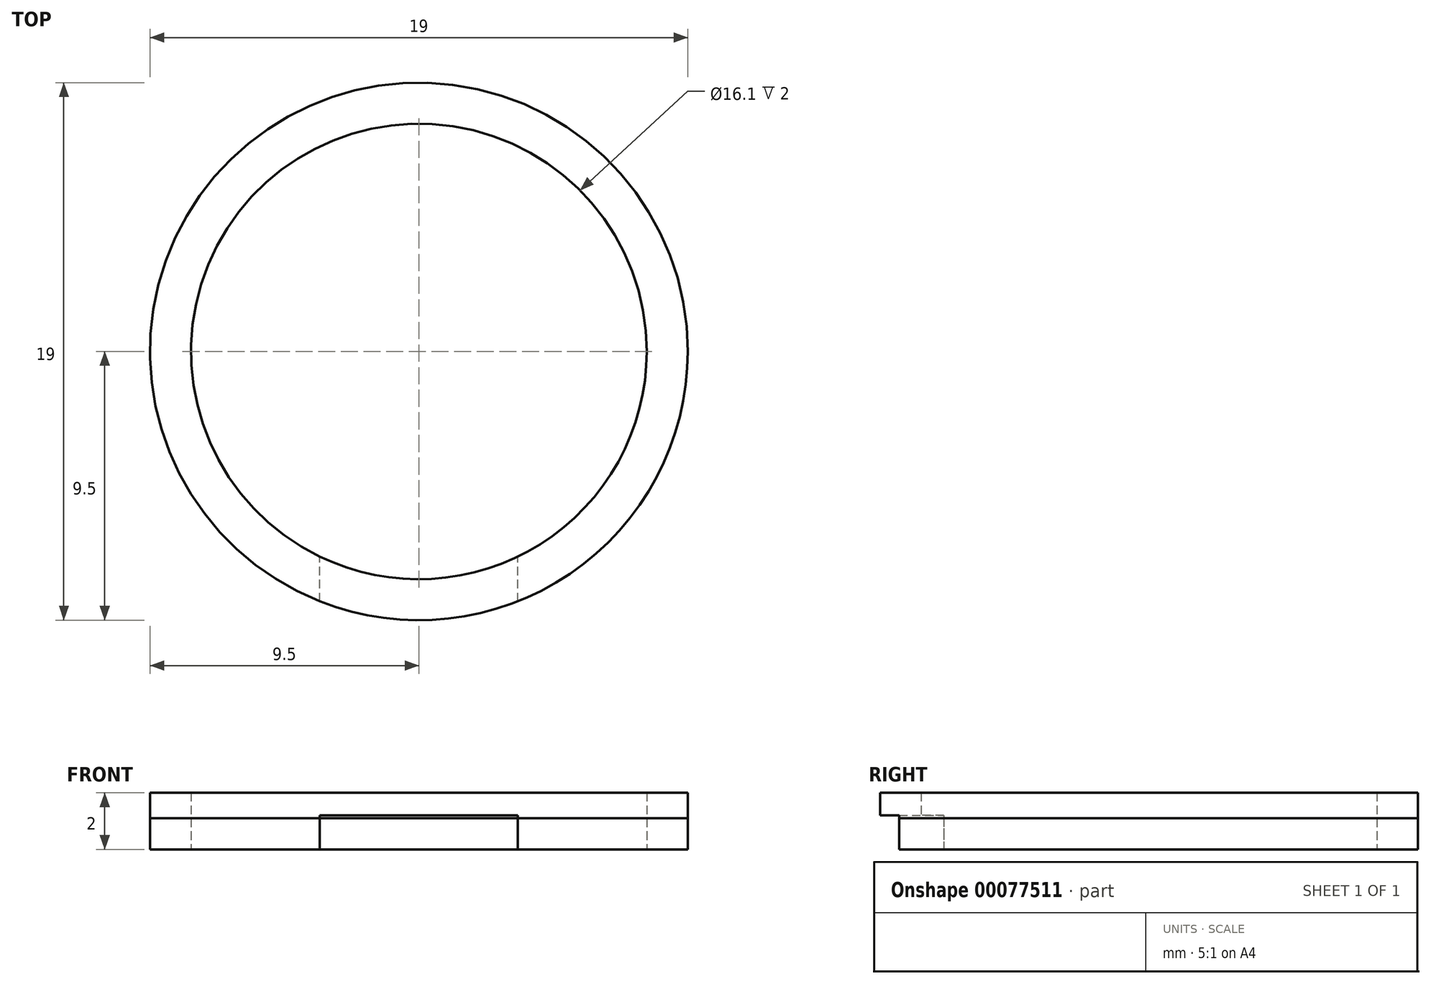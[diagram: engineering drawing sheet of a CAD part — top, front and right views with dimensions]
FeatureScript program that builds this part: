
annotation { "Feature Type Name" : "Feature", "Feature Type Description" : "" }
export const myFeature = defineFeature(function(context is Context, id is Id, definition is map)
    precondition{}
    {
        {
            var Q0;
            Q0=qCreatedBy(makeId("Top.planeOp"),FACE);
            var sketch = newSketch(context, id + "F0", { "sketchPlane" : qUnion([Q0])});
            skCircle(sketch, "E0", {"center": v(0, 0) * mm, "radius": 8.05 * mm});
            skCircle(sketch, "E1", {"center": v(0, 0) * mm, "radius": 9.5 * mm});
            skSolve(sketch);
        }
        {
            var Q0;
            Q0=makeQuery(id+"F0.imprint","IMPRINT",FACE,{"disambiguationData":[TD([[makeQuery(id+"F0.imprint","IMPRINT",EDGE,{"derivedFrom":sQuery(id+"F0.wireOp",EDGE,"E0")}),-1.0]])]});
            extrude(context, id + "F1", {"entities" : qUnion([Q0]), "depth" : 1.1 * mm});
        }
        {
            var Q0;
            Q0=makeQuery(id+"F0.imprint","IMPRINT",FACE,{"disambiguationData":[TD([[makeQuery(id+"F0.imprint","IMPRINT",EDGE,{"derivedFrom":sQuery(id+"F0.wireOp",EDGE,"E0")}),-1.0]])]});
            extrude(context, id + "F2", {"entities" : qUnion([Q0]), "depth" : 2 * mm});
        }
        {
            var Q0;
            Q0=makeQuery(id+"F2.opExtrude","CAP_FACE",FACE,{"disambiguationData":[OSD([sQuery(id+"F0.wireOp",EDGE,"E0"),sQuery(id+"F0.wireOp",EDGE,"E1")])],"isStart":true});
            var sketch = newSketch(context, id + "F3", { "sketchPlane" : qUnion([Q0])});
            skLineSegment(sketch, "E2", {"start": v(-3.5, 8.83) * mm, "end": v(-3.5, 7.25) * mm});
            skLineSegment(sketch, "E3", {"start": v(3.5, 8.83) * mm, "end": v(3.5, 7.25) * mm});
            skSolve(sketch);
        }
        {
            var Q0;
            {var subQ2=sQuery(id+"F3.wireOp",EDGE,"E2");Q0=makeQuery(id+"F3.imprint","IMPRINT",FACE,{"disambiguationData":[TD([[makeQuery(id+"F3.imprint","IMPRINT",EDGE,{"derivedFrom":subQ2}),1.0]])]});}
            extrude(context, id + "F4", {"entities" : qUnion([Q0]), "operationType" : NewBodyOperationType.REMOVE, "oppositeDirection" : true, "depth" : 1.2 * mm});
        }
    });
